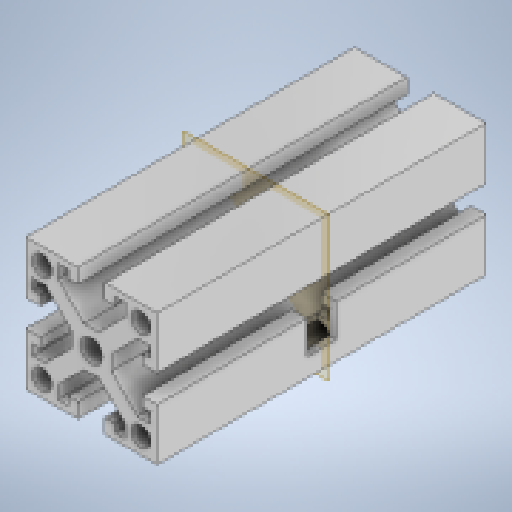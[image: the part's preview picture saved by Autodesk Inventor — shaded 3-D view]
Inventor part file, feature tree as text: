
AUTODESK INVENTOR PART (.ipt)
format: ipt  version: 2024.1 (Build 281209000, 209)  size: 345,088 bytes
history: native  units: in
note: dims shown in document units (in); Inventor stores cm internally (conversion verified against a paired STEP export)
features: reference x4, extrude x2, sketch x2, other x2, plane x1
ambient origin geometry x8: Origin, YZ Plane, XZ Plane, XY Plane, X Axis, Y Axis, Z Axis, Center Point
bodies: Solid1 (feature_tree)
feature tree (11):
  extrude  "Extrusion1"  TaperAngle=45.0deg  [1 undecoded]
  plane  "Work Plane1"
  extrude  "Extrusion2"  Depth=0.2362in
  sketch  "Sketch1"  dims[d0=0.2677in d1=45.0deg]
  sketch  "Sketch2"  dims[d2=0.7874in d3=0.2362in d4=0.5906in d5=0.4035in d6=0.2795in d7=0.1634in d8=0.1772in d9=0.0787in d10=0.5492in d11=0.2362in d12=1.5748in d14=360.0deg d16=3.9425in d17=0.0in d18=0.0108in d19=0.2362in d20=0.0in]
  reference  "Reference1"
  reference  "Reference2"
  reference  "Reference3"
  reference  "Reference4"
  other  "1_Base.iam"
  other  "HTD-45H:1"
note: 1 required parameter value undecoded (feature->parameter linkage not recoverable at this tier; creation-order binding heuristic only, values carry confidence <= 0.55)
